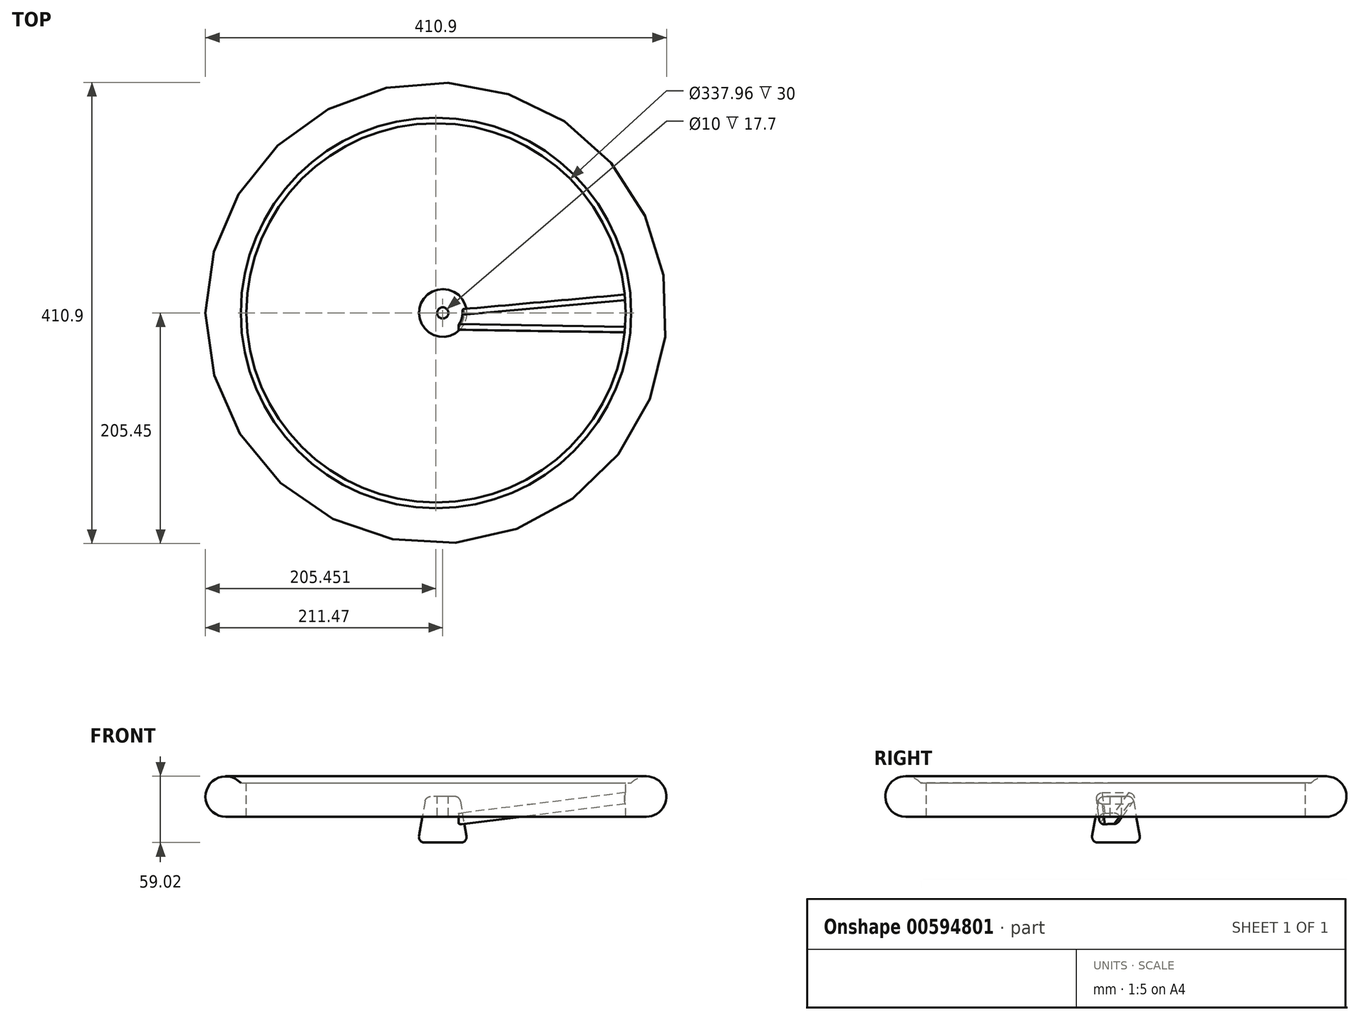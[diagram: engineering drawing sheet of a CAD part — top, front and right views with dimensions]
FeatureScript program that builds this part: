
annotation { "Feature Type Name" : "Feature", "Feature Type Description" : "" }
export const myFeature = defineFeature(function(context is Context, id is Id, definition is map)
    precondition{}
    {
        {
            var Q0;
            Q0=qCreatedBy(makeId("Top.planeOp"),FACE);
            var sketch = newSketch(context, id + "F0", { "sketchPlane" : qUnion([Q0])});
            skCircle(sketch, "E0", {"center": v(-6.02, 0) * mm, "radius": 190.5 * mm});
            skSolve(sketch);
        }
        {
            var Q0;
            Q0=qCreatedBy(makeId("Front.planeOp"),FACE);
            var sketch = newSketch(context, id + "F1", { "sketchPlane" : qUnion([Q0])});
            skArc(sketch, "E1", {"start": v(-180, 11.98) * mm, "mid": v(-209.89, 7.37) * mm, "end": v(-193.45, -18.02) * mm});
            skLineSegment(sketch, "E2", {"start": v(-180, 11.98) * mm, "end": v(-175, 11.98) * mm});
            skLineSegment(sketch, "E3", {"start": v(-175, 11.98) * mm, "end": v(-175, -18.02) * mm});
            skLineSegment(sketch, "E4", {"start": v(-175, -18.02) * mm, "end": v(-193.45, -18.02) * mm});
            skSolve(sketch);
        }
        {
            var Q0;
            Q0=makeQuery(id+"F1.imprint","IMPRINT",FACE,{"disambiguationData":[TD([[makeQuery(id+"F1.imprint","IMPRINT",EDGE,{"derivedFrom":sQuery(id+"F1.wireOp",EDGE,"E1")}),1.0]])]});
            var Q1;
            Q1=sQuery(id+"F0.wireOp",EDGE,"E0");
            sweep(context, id + "F2", {"profiles" : qUnion([Q0]), "path" : qUnion([Q1])});
        }
        {
            var Q0;
            Q0=qCreatedBy(makeId("Right.planeOp"),FACE);
            cPlane(context, id + "F3", {"entities" : qUnion([Q0]), "cplaneType" : CPlaneType.OFFSET, "offset" : 175 * mm, "width" : 150 * mm, "height" : 150 * mm});
        }
        {
            var Q0;
            Q0=qCreatedBy(id+"F3.planeOp",FACE);
            var sketch = newSketch(context, id + "F4", { "sketchPlane" : qUnion([Q0])});
            skLineSegment(sketch, "E5", {"start": v(-12.5, 0) * mm, "end": v(12.5, 0) * mm});
            skArc(sketch, "E6.0.startCap", {"start": v(-12.5, -5) * mm, "mid": v(-17.5, 0) * mm, "end": v(-12.5, 5) * mm});
            skArc(sketch, "E6.0.endCap", {"start": v(12.5, 5) * mm, "mid": v(17.5, 0) * mm, "end": v(12.5, -5) * mm});
            skLineSegment(sketch, "E6.0.left", {"start": v(-12.5, 5) * mm, "end": v(12.5, 5) * mm});
            skLineSegment(sketch, "E6.0.right", {"start": v(-12.5, -5) * mm, "end": v(12.5, -5) * mm});
            skSolve(sketch);
        }
        {
            var Q0;
            Q0=qCreatedBy(makeId("Right.planeOp"),FACE);
            cPlane(context, id + "F5", {"entities" : qUnion([Q0]), "cplaneType" : CPlaneType.OFFSET, "offset" : 14 * mm, "width" : 150 * mm, "height" : 150 * mm});
        }
        {
            var Q0;
            Q0=qCreatedBy(id+"F5.planeOp",FACE);
            var sketch = newSketch(context, id + "F6", { "sketchPlane" : qUnion([Q0])});
            skLineSegment(sketch, "E7", {"start": v(-10, -20) * mm, "end": v(-2, -20) * mm});
            skArc(sketch, "E8.0.startCap", {"start": v(-10, -25) * mm, "mid": v(-15, -20) * mm, "end": v(-10, -15) * mm});
            skArc(sketch, "E8.0.endCap", {"start": v(-2, -15) * mm, "mid": v(3, -20) * mm, "end": v(-2, -25) * mm});
            skLineSegment(sketch, "E8.0.left", {"start": v(-10, -15) * mm, "end": v(-2, -15) * mm});
            skLineSegment(sketch, "E8.0.right", {"start": v(-10, -25) * mm, "end": v(-2, -25) * mm});
            skSolve(sketch);
        }
        {
            var Q1;
            Q1 = qSketchRegion(id + "F4", true);
            var Q2;
            Q2 = qSketchRegion(id + "F6", true);
            loft(context, id + "F7", {"operationType" : NewBodyOperationType.ADD, "sheetProfilesArray" : [{ "sheetProfileEntities" : qUnion([Q1]) }, { "sheetProfileEntities" : qUnion([Q2]) }]});
        }
        {
            var Q0;
            Q0=qCreatedBy(makeId("Top.planeOp"),FACE);
            var sketch = newSketch(context, id + "F8", { "sketchPlane" : qUnion([Q0])});
            skCircle(sketch, "E9", {"center": v(0, 0) * mm, "radius": 15 * mm});
            skSolve(sketch);
        }
        {
            var Q0;
            Q0=makeQuery(id+"F8.imprint","IMPRINT",FACE,{"disambiguationData":[TD([[makeQuery(id+"F8.imprint","IMPRINT",EDGE,{"derivedFrom":sQuery(id+"F8.wireOp",EDGE,"E9")}),1.0]])]});
            extrude(context, id + "F9", {"entities" : qUnion([Q0]), "operationType" : NewBodyOperationType.ADD, "oppositeDirection" : true, "depth" : 41 * mm, "offsetDistance" : 25 * mm, "hasDraft" : true, "draftAngle" : 10 * degree});
        }
        {
            var Q0;
            Q0=qCreatedBy(makeId("Top.planeOp"),FACE);
            var sketch = newSketch(context, id + "F10", { "sketchPlane" : qUnion([Q0])});
            skCircle(sketch, "E10", {"center": v(0, 0) * mm, "radius": 5 * mm});
            skSolve(sketch);
        }
        {
            var Q0;
            Q0 = qSketchRegion(id + "F10", true);
            extrude(context, id + "F11", {"entities" : qUnion([Q0]), "operationType" : NewBodyOperationType.REMOVE, "oppositeDirection" : true, "depth" : 17.7 * mm, "offsetDistance" : 25 * mm});
        }
        {
            var Q0;
            Q0=makeQuery(id+"F9.opExtrude","CAP_EDGE",EDGE,{"disambiguationData":[OSD([sQuery(id+"F8.wireOp",EDGE,"E9")])],"isStart":true});
            var Q1;
            {var subQ0=sQuery(id+"F10.wireOp",EDGE,"E10");Q1=makeQuery(id+"F11.boolean.opBoolean","COPY",EDGE,{"disambiguationData":[topologyDisambiguationEdgeConnected([makeQuery(id+"Fy3zlsfpzRqvU03_1.opPattern","COPY",FACE,{"derivedFrom":makeQuery(id+"F9.opExtrude","CAP_FACE",FACE,{"disambiguationData":[OSD([sQuery(id+"F8.wireOp",EDGE,"E9")])],"isStart":true}),"instanceName":"4"})])],"derivedFrom":makeQuery(id+"F11.opExtrude","CAP_EDGE",EDGE,{"disambiguationData":[OSD([subQ0])],"isStart":true})});}
            var Q2;
            Q2=makeQuery(id+"F9.opExtrude","CAP_EDGE",EDGE,{"disambiguationData":[OSD([sQuery(id+"F8.wireOp",EDGE,"E9")])],"isStart":false});
            var Q3;
            Q3=makeQuery(id+"F11.boolean.opBoolean","INTERSECT",EDGE,{"derivedFrom":[makeQuery(id+"Fy3zlsfpzRqvU03_1.opPattern","COPY",FACE,{"derivedFrom":makeQuery(id+"F9.opExtrude","CAP_FACE",FACE,{"disambiguationData":[OSD([sQuery(id+"F8.wireOp",EDGE,"E9")])],"isStart":false}),"instanceName":"4"}),makeQuery(id+"F11.opExtrude","SWEPT_FACE",FACE,{"disambiguationData":[OSD([sQuery(id+"F10.wireOp",EDGE,"E10")])]})]});
            fillet(context, id + "F12", {"entities" : qUnion([Q0, Q1, Q2, Q3]), "radius" : 5 * mm, "tangentPropagation" : true, "allowEdgeOverflow" : false});
        }
    });
